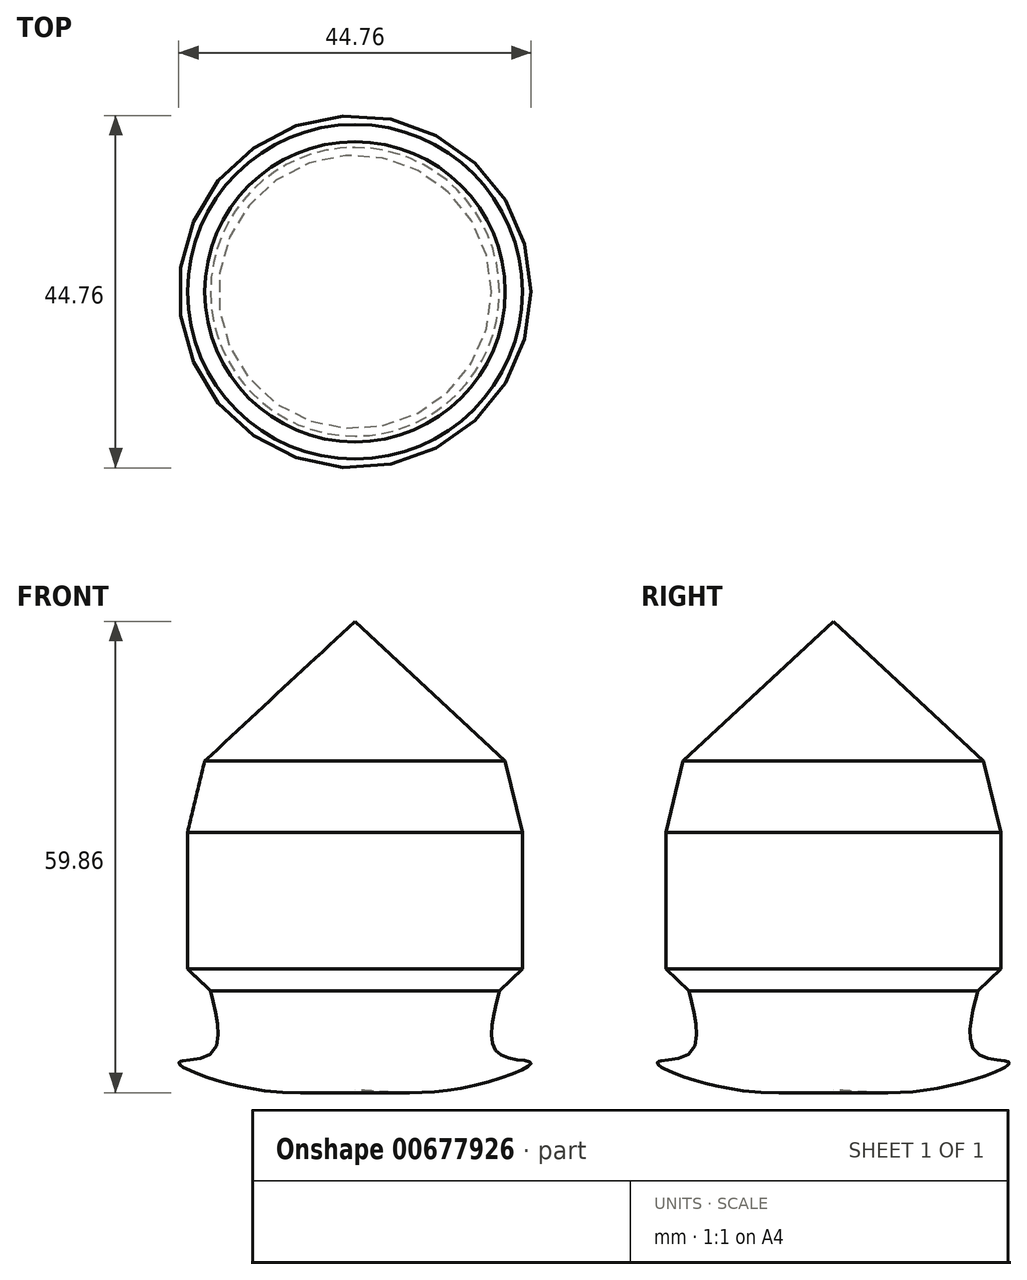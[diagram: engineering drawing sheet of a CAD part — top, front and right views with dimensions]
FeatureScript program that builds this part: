
annotation { "Feature Type Name" : "Feature", "Feature Type Description" : "" }
export const myFeature = defineFeature(function(context is Context, id is Id, definition is map)
    precondition{}
    {
        {
            var Q0;
            Q0=qCreatedBy(makeId("Front.planeOp"),FACE);
            var sketch = newSketch(context, id + "F0", { "sketchPlane" : qUnion([Q0])});
            skLineSegment(sketch, "E0", {"start": v(0, -30.48) * mm, "end": v(0, 36.32) * mm});
            skLineSegment(sketch, "E1", {"start": v(0, 29.02) * mm, "end": v(19.07, 11.32) * mm});
            skLineSegment(sketch, "E2", {"start": v(19.07, 11.32) * mm, "end": v(21.26, 2.2) * mm});
            skLineSegment(sketch, "E3", {"start": v(21.26, 2.2) * mm, "end": v(21.26, -6.39) * mm});
            skLineSegment(sketch, "E4", {"start": v(21.26, -6.39) * mm, "end": v(21.26, -15.15) * mm});
            skLineSegment(sketch, "E5", {"start": v(21.26, -15.15) * mm, "end": v(18.34, -17.89) * mm});
            skFitSpline(sketch, "E6", {"points": [v(18.34, -17.89) * mm, v(18.34, -25.92) * mm, v(22.36, -27.01) * mm, v(14.33, -30.11) * mm, v(0, -30.48) * mm], "startDerivative": vector(-10.42, -41.53) * mm, "endDerivative": vector(-42.02, 3.33) * mm});
            skSolve(sketch);
        }
        {
            var Q0;
            {var subQ0=sQuery(id+"F0.wireOp",EDGE,"E1");Q0=makeQuery(id+"F0.imprint","IMPRINT",FACE,{"disambiguationData":[TD([[makeQuery(id+"F0.imprint","IMPRINT",EDGE,{"derivedFrom":subQ0}),-1.0]])]});}
            var Q1;
            Q1=sQuery(id+"F0.wireOp",EDGE,"E0");
            revolve(context, id + "F1", {"entities" : qUnion([Q0]), "axis" : qUnion([Q1]), "revolveType" : RevolveType.FULL});
        }
    });
